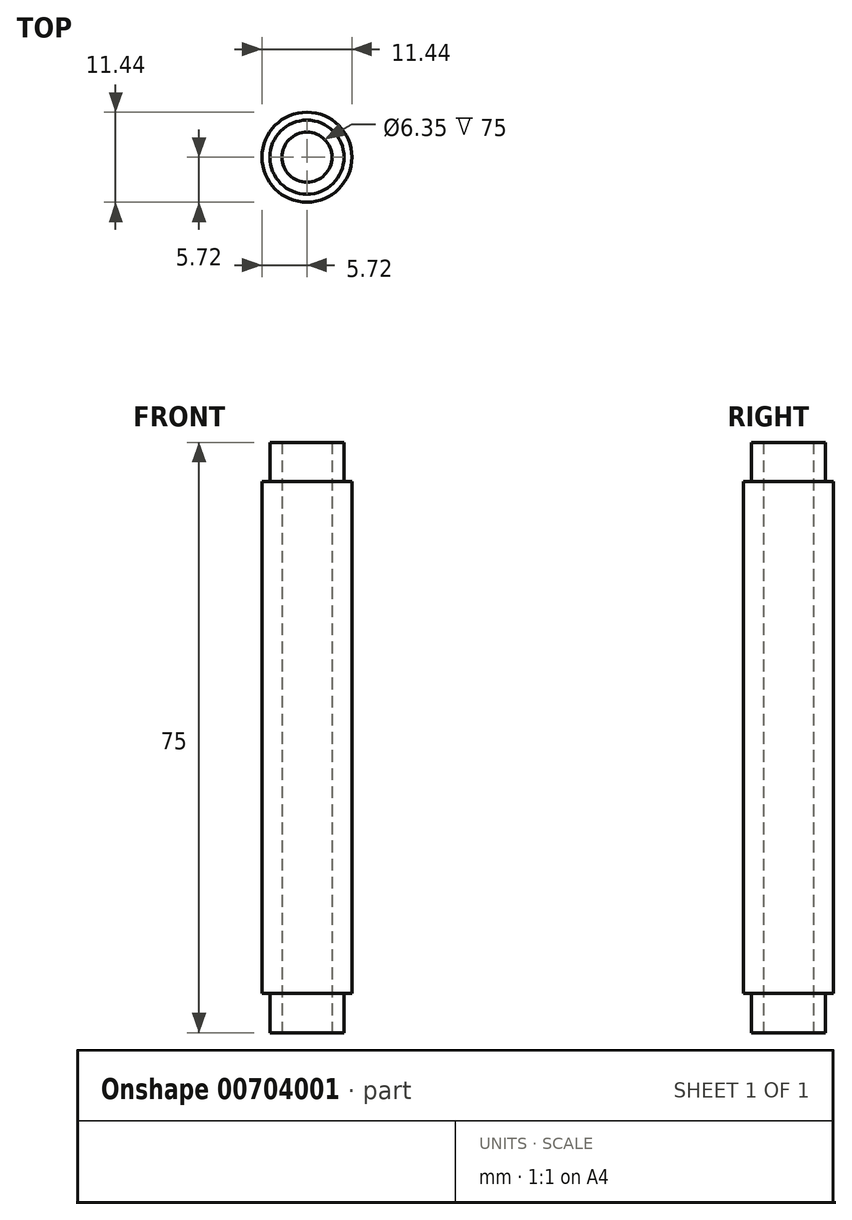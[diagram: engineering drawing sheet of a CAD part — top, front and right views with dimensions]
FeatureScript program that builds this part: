
annotation { "Feature Type Name" : "Feature", "Feature Type Description" : "" }
export const myFeature = defineFeature(function(context is Context, id is Id, definition is map)
    precondition{}
    {
        {
            var Q0;
            Q0=qCreatedBy(makeId("Top.planeOp"),FACE);
            var sketch = newSketch(context, id + "F0", { "sketchPlane" : qUnion([Q0])});
            skCircle(sketch, "E0", {"center": v(0, 0) * mm, "radius": 5.71 * mm});
            skCircle(sketch, "E1", {"center": v(0, 0) * mm, "radius": 3.18 * mm});
            skSolve(sketch);
        }
        {
            var Q0;
            Q0=makeQuery(id+"F0.imprint","IMPRINT",FACE,{"disambiguationData":[TD([[makeQuery(id+"F0.imprint","IMPRINT",EDGE,{"derivedFrom":sQuery(id+"F0.wireOp",EDGE,"E0")}),1.0]])]});
            extrude(context, id + "F1", {"entities" : qUnion([Q0]), "depth" : 75 * mm, "offsetDistance" : 25 * mm});
        }
        {
            var Q0;
            Q0=makeQuery(id+"F1.opExtrude","CAP_FACE",FACE,{"disambiguationData":[OSD([sQuery(id+"F0.wireOp",EDGE,"E0"),sQuery(id+"F0.wireOp",EDGE,"E1")])],"isStart":false});
            var sketch = newSketch(context, id + "F2", { "sketchPlane" : qUnion([Q0])});
            skCircle(sketch, "E2", {"center": v(0, 0) * mm, "radius": 5.71 * mm});
            skCircle(sketch, "E3", {"center": v(0, 0) * mm, "radius": 4.7 * mm});
            skSolve(sketch);
        }
        {
            var Q0;
            Q0 = qSketchRegion(id + "F2", true);
            extrude(context, id + "F3", {"entities" : qUnion([Q0]), "operationType" : NewBodyOperationType.REMOVE, "oppositeDirection" : true, "depth" : 5 * mm, "offsetDistance" : 25 * mm});
        }
        {
            var Q0;
            Q0=makeQuery(id+"F1.opExtrude","CAP_FACE",FACE,{"disambiguationData":[OSD([sQuery(id+"F0.wireOp",EDGE,"E0"),sQuery(id+"F0.wireOp",EDGE,"E1")])],"isStart":true});
            var sketch = newSketch(context, id + "F4", { "sketchPlane" : qUnion([Q0])});
            skCircle(sketch, "E4", {"center": v(0, 0) * mm, "radius": 5.71 * mm});
            skCircle(sketch, "E5", {"center": v(0, 0) * mm, "radius": 4.7 * mm});
            skSolve(sketch);
        }
        {
            var Q0;
            Q0 = qSketchRegion(id + "F4", true);
            extrude(context, id + "F5", {"entities" : qUnion([Q0]), "operationType" : NewBodyOperationType.REMOVE, "oppositeDirection" : true, "depth" : 5 * mm, "offsetDistance" : 25 * mm});
        }
    });
